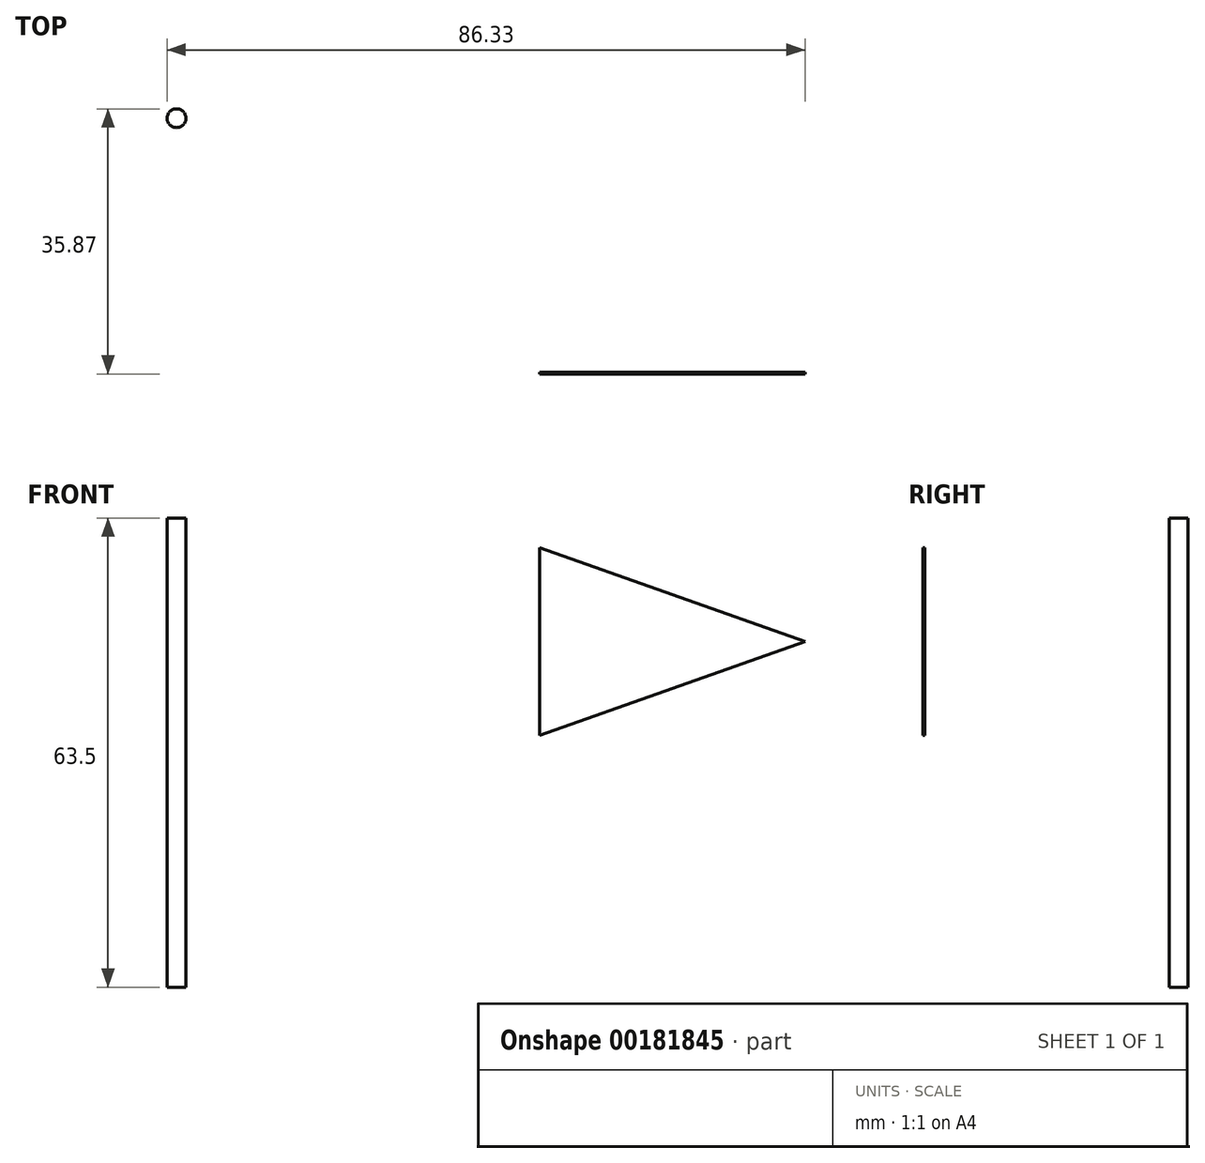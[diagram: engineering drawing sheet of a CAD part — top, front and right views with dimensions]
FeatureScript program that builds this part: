
annotation { "Feature Type Name" : "Feature", "Feature Type Description" : "" }
export const myFeature = defineFeature(function(context is Context, id is Id, definition is map)
    precondition{}
    {
        {
            var Q0;
            Q0=qCreatedBy(makeId("Top.planeOp"),FACE);
            var sketch = newSketch(context, id + "F0", { "sketchPlane" : qUnion([Q0])});
            skCircle(sketch, "E0", {"center": v(-35.46, 34.35) * mm, "radius": 1.27 * mm});
            skSolve(sketch);
        }
        {
            var Q0;
            Q0=makeQuery(id+"F0.imprint","IMPRINT",FACE,{"disambiguationData":[TD([[makeQuery(id+"F0.imprint","IMPRINT",EDGE,{"derivedFrom":sQuery(id+"F0.wireOp",EDGE,"E0")}),1.0]])]});
            extrude(context, id + "F1", {"entities" : qUnion([Q0]), "depth" : 63.5 * mm});
        }
        {
            var Q0;
            Q0=qCreatedBy(makeId("Front.planeOp"),FACE);
            var sketch = newSketch(context, id + "F2", { "sketchPlane" : qUnion([Q0])});
            skLineSegment(sketch, "E1", {"start": v(13.68, 59.46) * mm, "end": v(13.68, 34.06) * mm});
            skLineSegment(sketch, "E2", {"start": v(13.68, 34.06) * mm, "end": v(49.6, 46.76) * mm});
            skLineSegment(sketch, "E3", {"start": v(49.6, 46.76) * mm, "end": v(13.68, 59.46) * mm});
            skSolve(sketch);
        }
        {
            var Q0;
            Q0=makeQuery(id+"F2.imprint","IMPRINT",FACE,{"disambiguationData":[TD([[makeQuery(id+"F2.imprint","IMPRINT",EDGE,{"derivedFrom":sQuery(id+"F2.wireOp",EDGE,"E1")}),1.0]])]});
            extrude(context, id + "F3", {"entities" : qUnion([Q0]), "depth" : 0.25 * mm});
        }
    });
